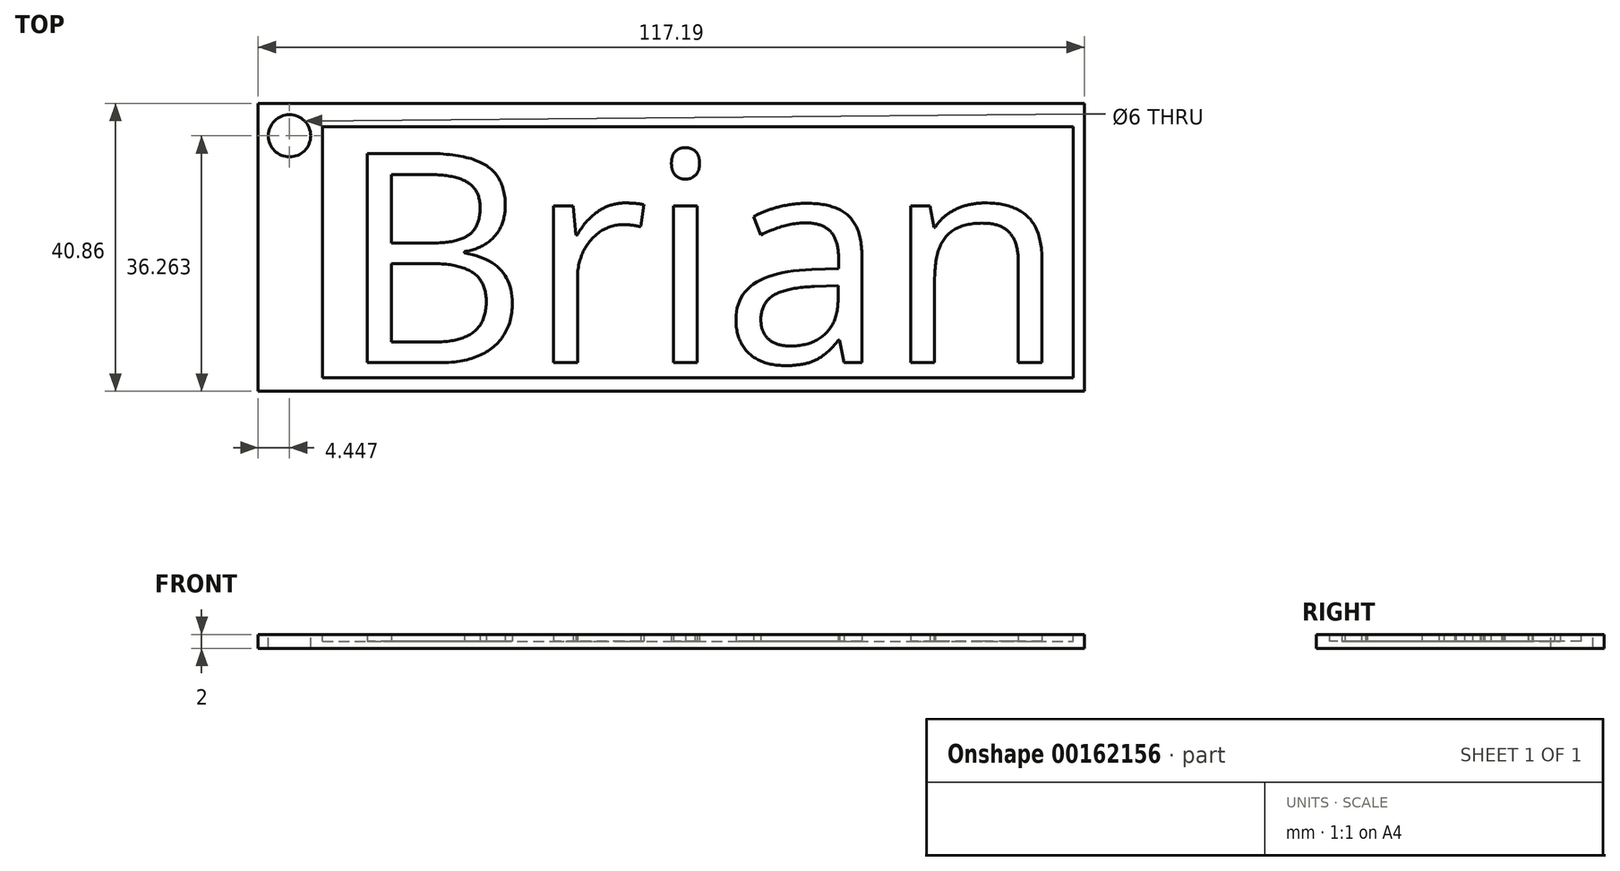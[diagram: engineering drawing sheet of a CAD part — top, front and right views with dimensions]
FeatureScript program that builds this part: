
annotation { "Feature Type Name" : "Feature", "Feature Type Description" : "" }
export const myFeature = defineFeature(function(context is Context, id is Id, definition is map)
    precondition{}
    {
        {
            var Q0;
            Q0=qCreatedBy(makeId("Top.planeOp"),FACE);
            var sketch = newSketch(context, id + "F0", { "sketchPlane" : qUnion([Q0])});
            skLineSegment(sketch, "E0.bottom", {"start": v(-56.51, 30.16) * mm, "end": v(55.18, 30.16) * mm});
            skLineSegment(sketch, "E0.top", {"start": v(-56.51, -20.45) * mm, "end": v(55.18, -20.45) * mm});
            skLineSegment(sketch, "E0.left", {"start": v(-56.51, 30.16) * mm, "end": v(-56.51, -20.45) * mm});
            skLineSegment(sketch, "E0.right", {"start": v(55.18, 30.16) * mm, "end": v(55.18, -20.45) * mm});
            skSolve(sketch);
        }
        {
            var Q0;
            Q0=makeQuery(id+"F0.imprint","IMPRINT",FACE,{"disambiguationData":[TD([[makeQuery(id+"F0.imprint","IMPRINT",EDGE,{"derivedFrom":sQuery(id+"F0.wireOp",EDGE,"E0.bottom")}),-1.0]])]});
            extrude(context, id + "F1", {"entities" : qUnion([Q0]), "depth" : 2 * mm});
        }
        {
            var Q0;
            Q0=makeQuery(id+"F1.opExtrude","CAP_FACE",FACE,{"disambiguationData":[OSD([sQuery(id+"F0.wireOp",EDGE,"E0.bottom"),sQuery(id+"F0.wireOp",EDGE,"E0.top"),sQuery(id+"F0.wireOp",EDGE,"E0.left"),sQuery(id+"F0.wireOp",EDGE,"E0.right")])],"isStart":false});
            var sketch = newSketch(context, id + "F2", { "sketchPlane" : qUnion([Q0])});
            skCircle(sketch, "E1", {"center": v(-52.06, 25.56) * mm, "radius": 3 * mm});
            skSolve(sketch);
        }
        {
            var Q0;
            Q0 = qSketchRegion(id + "F2", true);
            extrude(context, id + "F3", {"entities" : qUnion([Q0]), "operationType" : NewBodyOperationType.REMOVE, "oppositeDirection" : true, "depth" : 25 * mm});
        }
        {
            var Q0;
            Q0=makeQuery(id+"F1.opExtrude","CAP_FACE",FACE,{"disambiguationData":[OSD([sQuery(id+"F0.wireOp",EDGE,"E0.bottom"),sQuery(id+"F0.wireOp",EDGE,"E0.top"),sQuery(id+"F0.wireOp",EDGE,"E0.left"),sQuery(id+"F0.wireOp",EDGE,"E0.right")])],"isStart":false});
            var sketch = newSketch(context, id + "F4", { "sketchPlane" : qUnion([Q0])});
            skLineSegment(sketch, "E2.bottom", {"start": v(-47.38, 26.87) * mm, "end": v(53.37, 26.87) * mm});
            skLineSegment(sketch, "E2.top", {"start": v(-47.38, -18.26) * mm, "end": v(53.37, -18.26) * mm});
            skLineSegment(sketch, "E2.left", {"start": v(-47.38, 26.87) * mm, "end": v(-47.38, -18.26) * mm});
            skLineSegment(sketch, "E2.right", {"start": v(53.37, 26.87) * mm, "end": v(53.37, -18.26) * mm});
            skSolve(sketch);
        }
        {
            var Q0;
            Q0=makeQuery(id+"F4.imprint","IMPRINT",FACE,{"disambiguationData":[TD([[makeQuery(id+"F4.imprint","IMPRINT",EDGE,{"derivedFrom":sQuery(id+"F4.wireOp",EDGE,"E2.bottom")}),-1.0]])]});
            extrude(context, id + "F5", {"entities" : qUnion([Q0]), "operationType" : NewBodyOperationType.REMOVE, "oppositeDirection" : true, "depth" : 1 * mm});
        }
        {
            var Q0;
            Q0=makeQuery(id+"F5.boolean.opBoolean","COPY",FACE,{"derivedFrom":makeQuery(id+"F5.opExtrude","CAP_FACE",FACE,{"disambiguationData":[OSD([sQuery(id+"F4.wireOp",EDGE,"E2.bottom"),sQuery(id+"F4.wireOp",EDGE,"E2.top"),sQuery(id+"F4.wireOp",EDGE,"E2.left"),sQuery(id+"F4.wireOp",EDGE,"E2.right")])],"isStart":false})});
            var sketch = newSketch(context, id + "F6", { "sketchPlane" : qUnion([Q0])});
            skText(sketch, "E3", { "text": "Brian", "fontName": "OpenSans-Regular.ttf"});
            const initialGuessF6  = {"E3": [-0.04513, -0.00665, 1, 0, 0.02996]};
            skSetInitialGuess(sketch, initialGuessF6);
            skSolve(sketch);
        }
        {
            var Q0;
            Q0=makeQuery(id+"F1.opExtrude","SWEPT_FACE",FACE,{"disambiguationData":[OSD([sQuery(id+"F0.wireOp",EDGE,"E0.right")])]});
            extrude(context, id + "F7", {"entities" : qUnion([Q0]), "operationType" : NewBodyOperationType.ADD, "depth" : 5.5 * mm});
        }
        {
            var Q0;
            Q0=makeQuery(id+"F5.boolean.opBoolean","COPY",FACE,{"derivedFrom":makeQuery(id+"F5.opExtrude","SWEPT_FACE",FACE,{"disambiguationData":[OSD([sQuery(id+"F4.wireOp",EDGE,"E2.right")])]})});
            extrude(context, id + "F8", {"entities" : qUnion([Q0]), "operationType" : NewBodyOperationType.REMOVE, "oppositeDirection" : true, "depth" : 5.75 * mm});
        }
        {
            var Q0;
            Q0 = qSketchRegion(id + "F6", true);
            extrude(context, id + "F9", {"entities" : qUnion([Q0]), "operationType" : NewBodyOperationType.ADD, "depth" : 1 * mm});
        }
        {
            var Q0;
            {var subQ0=sQuery(id+"F4.wireOp",EDGE,"E2.top");Q0=makeQuery(id+"F8.boolean.opBoolean","MERGE",FACE,{"derivedFrom":[makeQuery(id+"F5.boolean.opBoolean","COPY",FACE,{"derivedFrom":makeQuery(id+"F5.opExtrude","SWEPT_FACE",FACE,{"disambiguationData":[OSD([subQ0])]})}),makeQuery(id+"F8.opExtrude","SWEPT_FACE",FACE,{"disambiguationData":[OSD([subQ0,sQuery(id+"F4.wireOp",EDGE,"E2.right")])]})]});}
            extrude(context, id + "F10", {"entities" : qUnion([Q0]), "operationType" : NewBodyOperationType.ADD, "depth" : 9.5 * mm});
        }
        {
            var Q0;
            {var subQ0=sQuery(id+"F0.wireOp",EDGE,"E0.top");Q0=makeQuery(id+"F7.boolean.opBoolean","MERGE",FACE,{"derivedFrom":[makeQuery(id+"F1.opExtrude","SWEPT_FACE",FACE,{"disambiguationData":[OSD([subQ0])]}),makeQuery(id+"F7.opExtrude","SWEPT_FACE",FACE,{"disambiguationData":[OSD([subQ0,sQuery(id+"F0.wireOp",EDGE,"E0.right")])]})]});}
            extrude(context, id + "F11", {"entities" : qUnion([Q0]), "operationType" : NewBodyOperationType.REMOVE, "oppositeDirection" : true, "depth" : 9.75 * mm});
        }
    });
